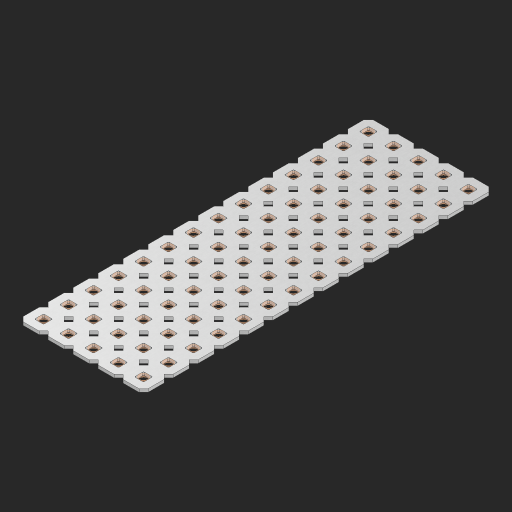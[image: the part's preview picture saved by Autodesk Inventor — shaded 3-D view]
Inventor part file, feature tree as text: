
AUTODESK INVENTOR PART (.ipt)
format: ipt  version: 2023 (Build 270158000, 158)  size: 1,096,704 bytes
history: native  units: in
note: dims shown in document units (in); Inventor stores cm internally (conversion verified against a paired STEP export)
features: other x71, extrude x69, sketch x2, pattern_linear x1
ambient origin geometry x8: Origin, YZ Plane, XZ Plane, XY Plane, X Axis, Y Axis, Z Axis, Center Point
bodies: Solid1 (feature_tree), Body (feature_tree)
feature tree (143):
  pattern_linear  "Rectangular Pattern1"  Spacing1=0.09in  [1 undecoded]
  sketch  "Sketch1"  dims[d1=0.5in]
  sketch  "Sketch2"  dims[d2=0.182in d3=0.09in d4=0.09in d5=0.09in d6=0.09in d7=0.09in d8=0.09in d9=0.09in d10=0.09in d11=0.02in d13=0.0in d14=0.172in d15=0.0625in d16=0.0in d19=0.5in d22=0.5in]
  other  "Srf1"
  other  "Srf126"
  other  "Srf127"
  other  "Srf128"
  other  "Srf129"
  other  "Srf130"
  other  "Srf131"
  other  "Srf250"
  other  "Srf251"
  other  "Srf252"
  other  "Srf253"
  other  "Srf254"
  other  "Srf255"
  other  "Srf256"
  other  "Srf268"
  other  "Srf269"
  other  "Srf270"
  other  "Srf271"
  other  "Srf272"
  other  "Srf273"
  other  "Srf274"
  other  "Srf275"
  other  "Srf276"
  other  "Srf277"
  other  "Srf278"
  other  "Srf279"
  other  "Srf280"
  other  "Srf281"
  other  "Srf293"
  other  "Srf294"
  other  "Srf295"
  other  "Srf296"
  other  "Srf297"
  other  "Srf298"
  other  "Srf299"
  other  "Srf300"
  other  "Srf301"
  other  "Srf302"
  other  "Srf303"
  other  "Srf304"
  other  "Srf305"
  other  "Srf306"
  other  "Srf318"
  other  "Srf319"
  other  "Srf320"
  other  "Srf321"
  other  "Srf322"
  other  "Srf323"
  other  "Srf324"
  other  "Srf325"
  other  "Srf326"
  other  "Srf327"
  other  "Srf328"
  other  "Srf329"
  other  "Srf330"
  other  "Srf331"
  other  "Srf343"
  other  "Srf344"
  other  "Srf345"
  other  "Srf346"
  other  "Srf347"
  other  "Srf348"
  other  "Srf349"
  other  "Srf350"
  other  "Srf351"
  other  "Srf352"
  other  "Srf353"
  other  "Srf354"
  other  "Srf355"
  other  "Srf356"
  other  "Circle"
  extrude  "ExtrusionSrf126"  Depth=0.09in
  extrude  "ExtrusionSrf127"  Depth=0.09in
  extrude  "ExtrusionSrf128"  Depth=0.09in
  extrude  "ExtrusionSrf129"  Depth=0.09in
  extrude  "ExtrusionSrf130"  Depth=0.09in
  extrude  "ExtrusionSrf131"  Depth=0.09in
  extrude  "ExtrusionSrf250"  Depth=0.09in
  extrude  "ExtrusionSrf251"  Depth=0.02in
  extrude  "ExtrusionSrf252"  TaperAngle=0.0deg  [1 undecoded]
  extrude  "ExtrusionSrf253"  Depth=0.5in
  extrude  "ExtrusionSrf254"  Depth=0.0625in TaperAngle=0.0deg
  extrude  "ExtrusionSrf255"  Depth=0.5in
  extrude  "ExtrusionSrf256"  Depth=0.5in
  extrude  "ExtrusionSrf268"  [1 undecoded]
  extrude  "ExtrusionSrf269"  [1 undecoded]
  extrude  "ExtrusionSrf270"  [1 undecoded]
  extrude  "ExtrusionSrf271"  [1 undecoded]
  extrude  "ExtrusionSrf272"  [1 undecoded]
  extrude  "ExtrusionSrf273"  [1 undecoded]
  extrude  "ExtrusionSrf274"  [1 undecoded]
  extrude  "ExtrusionSrf275"  [1 undecoded]
  extrude  "ExtrusionSrf276"  [1 undecoded]
  extrude  "ExtrusionSrf277"  [1 undecoded]
  extrude  "ExtrusionSrf278"  [1 undecoded]
  extrude  "ExtrusionSrf279"  [1 undecoded]
  extrude  "ExtrusionSrf280"  [1 undecoded]
  extrude  "ExtrusionSrf281"  [1 undecoded]
  extrude  "ExtrusionSrf293"  [1 undecoded]
  extrude  "ExtrusionSrf294"  [1 undecoded]
  extrude  "ExtrusionSrf295"  [1 undecoded]
  extrude  "ExtrusionSrf296"  [1 undecoded]
  extrude  "ExtrusionSrf297"  [1 undecoded]
  extrude  "ExtrusionSrf298"  [1 undecoded]
  extrude  "ExtrusionSrf299"  [1 undecoded]
  extrude  "ExtrusionSrf300"  [1 undecoded]
  extrude  "ExtrusionSrf301"  [1 undecoded]
  extrude  "ExtrusionSrf302"  [1 undecoded]
  extrude  "ExtrusionSrf303"  [1 undecoded]
  extrude  "ExtrusionSrf304"  [1 undecoded]
  extrude  "ExtrusionSrf305"  [1 undecoded]
  extrude  "ExtrusionSrf306"  [1 undecoded]
  extrude  "ExtrusionSrf318"  [1 undecoded]
  extrude  "ExtrusionSrf319"  [1 undecoded]
  extrude  "ExtrusionSrf320"  [1 undecoded]
  extrude  "ExtrusionSrf321"  [1 undecoded]
  extrude  "ExtrusionSrf322"  [1 undecoded]
  extrude  "ExtrusionSrf323"  [1 undecoded]
  extrude  "ExtrusionSrf324"  [1 undecoded]
  extrude  "ExtrusionSrf325"  [1 undecoded]
  extrude  "ExtrusionSrf326"  [1 undecoded]
  extrude  "ExtrusionSrf327"  [1 undecoded]
  extrude  "ExtrusionSrf328"  [1 undecoded]
  extrude  "ExtrusionSrf329"  [1 undecoded]
  extrude  "ExtrusionSrf330"  [1 undecoded]
  extrude  "ExtrusionSrf331"  [1 undecoded]
  extrude  "ExtrusionSrf343"  [1 undecoded]
  extrude  "ExtrusionSrf344"  [1 undecoded]
  extrude  "ExtrusionSrf345"  [1 undecoded]
  extrude  "ExtrusionSrf346"  [1 undecoded]
  extrude  "ExtrusionSrf347"  [1 undecoded]
  extrude  "ExtrusionSrf348"  [1 undecoded]
  extrude  "ExtrusionSrf349"  [1 undecoded]
  extrude  "ExtrusionSrf350"  [1 undecoded]
  extrude  "ExtrusionSrf351"  [1 undecoded]
  extrude  "ExtrusionSrf352"  [1 undecoded]
  extrude  "ExtrusionSrf353"  [1 undecoded]
  extrude  "ExtrusionSrf354"  [1 undecoded]
  extrude  "ExtrusionSrf355"  [1 undecoded]
  extrude  "ExtrusionSrf356"  [1 undecoded]
note: 58 required parameter values undecoded (feature->parameter linkage not recoverable at this tier; creation-order binding heuristic only, values carry confidence <= 0.55)
